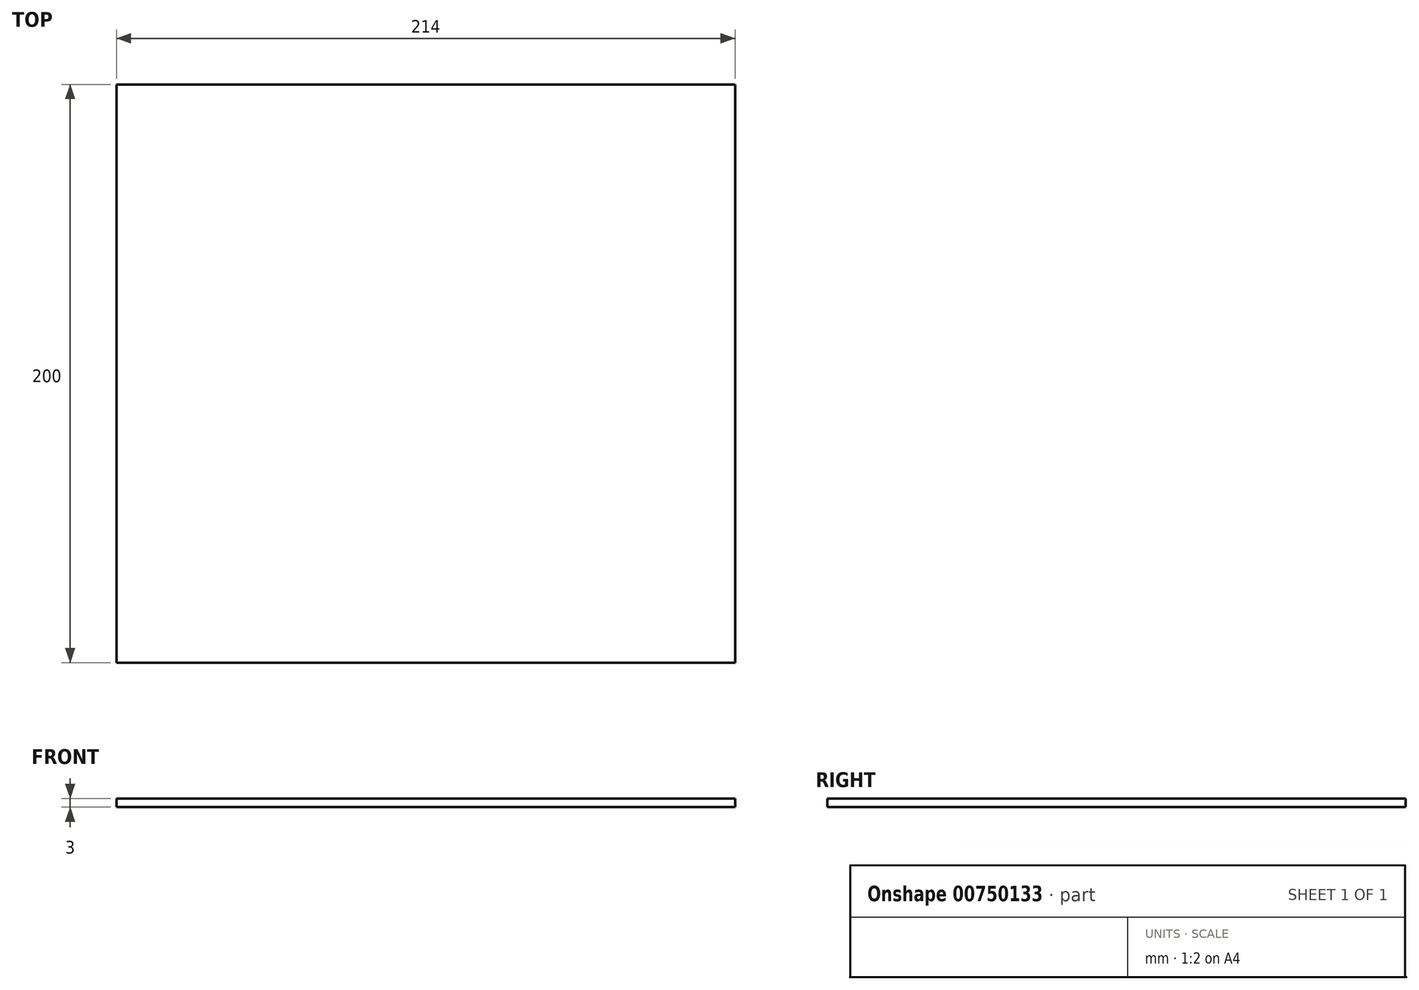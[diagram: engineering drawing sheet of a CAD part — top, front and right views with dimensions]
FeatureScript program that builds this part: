
annotation { "Feature Type Name" : "Feature", "Feature Type Description" : "" }
export const myFeature = defineFeature(function(context is Context, id is Id, definition is map)
    precondition{}
    {
        {
            var Q0;
            Q0=qCreatedBy(makeId("Top.planeOp"),FACE);
            var sketch = newSketch(context, id + "F0", { "sketchPlane" : qUnion([Q0])});
            skLineSegment(sketch, "E0.bottom", {"start": v(107, 100) * mm, "end": v(-107, 100) * mm});
            skLineSegment(sketch, "E0.top", {"start": v(107, -100) * mm, "end": v(-107, -100) * mm});
            skLineSegment(sketch, "E0.left", {"start": v(107, 100) * mm, "end": v(107, -100) * mm});
            skLineSegment(sketch, "E0.right", {"start": v(-107, 100) * mm, "end": v(-107, -100) * mm});
            skPoint(sketch, "E0.middle", {"position": v(0, 0) * mm});
            skSolve(sketch);
        }
        {
            var Q0;
            Q0=makeQuery(id+"F0.imprint","IMPRINT",FACE,{"disambiguationData":[TD([[makeQuery(id+"F0.imprint","IMPRINT",EDGE,{"derivedFrom":sQuery(id+"F0.wireOp",EDGE,"E0.bottom")}),1.0]])]});
            extrude(context, id + "F1", {"entities" : qUnion([Q0]), "depth" : 3 * mm, "offsetDistance" : 25 * mm});
        }
    });
